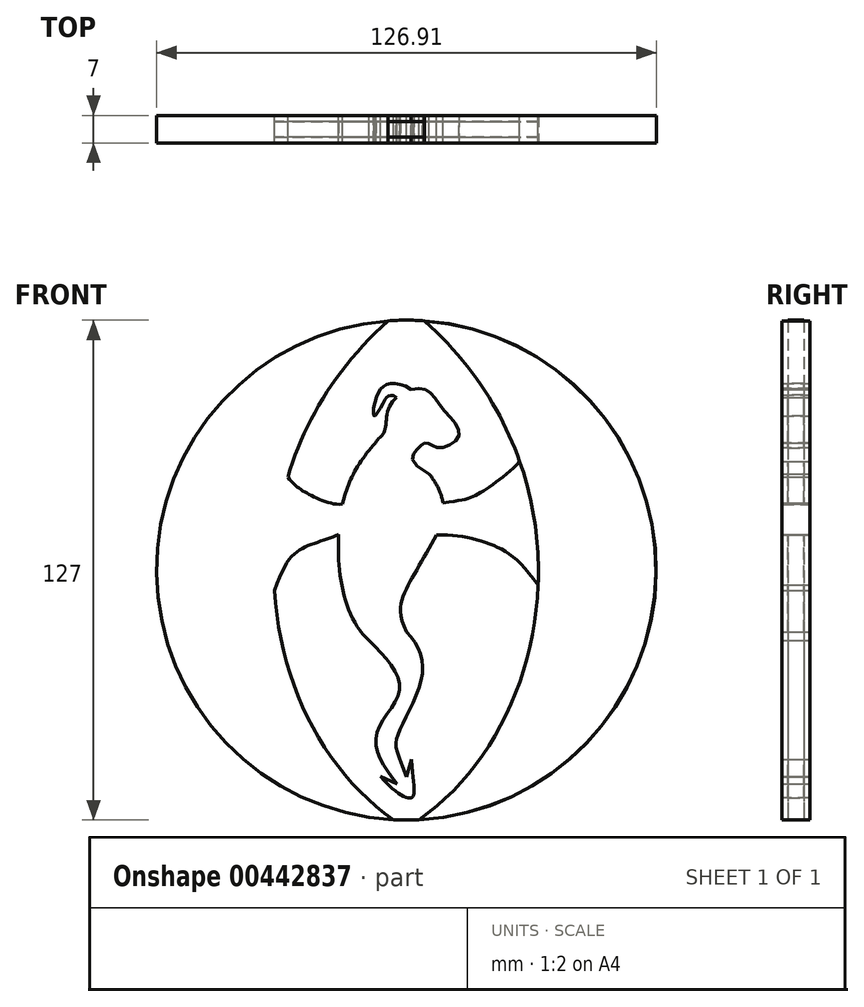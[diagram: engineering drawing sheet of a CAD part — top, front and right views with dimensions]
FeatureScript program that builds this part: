
annotation { "Feature Type Name" : "Feature", "Feature Type Description" : "" }
export const myFeature = defineFeature(function(context is Context, id is Id, definition is map)
    precondition{}
    {
        {
            var Q0;
            Q0=qCreatedBy(makeId("Front.planeOp"),FACE);
            var sketch = newSketch(context, id + "F0", { "sketchPlane" : qUnion([Q0])});
            skFitSpline(sketch, "E0", {"points": [v(-4.63, 63.33) * mm, v(-3.25, -63.42) * mm], "startDerivative": vector(-131.7, -118.32) * mm, "endDerivative": vector(104.02, -72.51) * mm});
            skFitSpline(sketch, "E1.MirrorCS", {"points": [v(4.63, 63.33) * mm, v(3.25, -63.42) * mm], "startDerivative": vector(131.7, -118.32) * mm, "endDerivative": vector(-104.02, -72.51) * mm});
            skFitSpline(sketch, "E2.MirrorCS", {"points": [v(4.63, 63.33) * mm, v(3.25, -63.42) * mm], "startDerivative": vector(131.7, -118.32) * mm, "endDerivative": vector(-104.02, -72.51) * mm});
            skFitSpline(sketch, "E3", {"points": [v(-7.83, 32.3) * mm, v(-17.25, 7.4) * mm, v(-9.48, -17.82) * mm], "startDerivative": vector(-42.51, -46.16) * mm, "endDerivative": vector(37.02, -32.66) * mm});
            skFitSpline(sketch, "E4", {"points": [v(0, -15.67) * mm, v(0, -4.86) * mm, v(6.45, 6.64) * mm, v(5.82, 24.48) * mm], "startDerivative": vector(-23.7, 51.33) * mm, "endDerivative": vector(-47.57, 61.34) * mm});
            skFitSpline(sketch, "E5", {"points": [v(-9.48, -17.82) * mm, v(-1.7, -30.34) * mm, v(-7.58, -41.9) * mm, v(-2.33, -54.32) * mm], "startDerivative": vector(35.97, -36.32) * mm, "endDerivative": vector(29.4, -36.63) * mm});
            skFitSpline(sketch, "E6", {"points": [v(0, -15.67) * mm, v(3.98, -26.92) * mm, v(-2.09, -41.71) * mm, v(0, -52.52) * mm], "startDerivative": vector(29.36, -30.45) * mm, "endDerivative": vector(25.51, -67.43) * mm});
            skLineSegment(sketch, "E7", {"start": v(-2.33, -54.32) * mm, "end": v(-6.5, -52.43) * mm});
            skLineSegment(sketch, "E8", {"start": v(0, -52.52) * mm, "end": v(1.33, -48.14) * mm});
            skFitSpline(sketch, "E9", {"points": [v(1.33, -48.14) * mm, v(1.33, -57.83) * mm, v(-6.5, -52.43) * mm], "startDerivative": vector(3.4, -40.84) * mm, "endDerivative": vector(-24.27, 27.98) * mm});
            skFitSpline(sketch, "E10", {"points": [v(-7.83, 32.3) * mm, v(-5.62, 34.96) * mm, v(-3.92, 42.22) * mm, v(4.16, 46.08) * mm, v(9.11, 41.2) * mm, v(13.41, 34.31) * mm, v(8.38, 31.08) * mm, v(5.3, 32.3) * mm, v(2.72, 30.66) * mm, v(5.82, 24.48) * mm], "startDerivative": vector(21.81, 45.2) * mm, "endDerivative": vector(144.1, -69.65) * mm});
            skFitSpline(sketch, "E11", {"points": [v(-16.2, 16.75) * mm, v(-24.84, 19.34) * mm, v(-30.09, 23.68) * mm], "startDerivative": vector(-16.82, -1.59) * mm, "endDerivative": vector(-11.22, 15.25) * mm});
            skFitSpline(sketch, "E12", {"points": [v(-17.2, 9.09) * mm, v(-24.84, 6.26) * mm, v(-33.44, -5.18) * mm], "startDerivative": vector(-15, -8.06) * mm, "endDerivative": vector(-14.25, -42.92) * mm});
            skFitSpline(sketch, "E13", {"points": [v(9.33, 17.07) * mm, v(18.58, 19.53) * mm, v(28.82, 27.58) * mm], "startDerivative": vector(36.83, 4.77) * mm, "endDerivative": vector(17.6, 18.89) * mm});
            skFitSpline(sketch, "E14", {"points": [v(7.7, 8.96) * mm, v(21.23, 6.64) * mm, v(33.5, -3.83) * mm], "startDerivative": vector(32.17, 0.55) * mm, "endDerivative": vector(27.66, -39.22) * mm});
            skFitSpline(sketch, "E15", {"points": [v(1.25, 45.88) * mm, v(-5, 47.14) * mm, v(-7.56, 44.07) * mm, v(-8.14, 39.17) * mm, v(-5.58, 42.97) * mm, v(-4.42, 44.27) * mm, v(-2.47, 43.9) * mm], "startDerivative": vector(-33.98, 22.97) * mm, "endDerivative": vector(16.3, -16.51) * mm});
            skArc(sketch, "E16", {"start": v(-4.63, 63.33) * mm, "mid": v(-63.41, -0.7) * mm, "end": v(-3.25, -63.42) * mm});
            skArc(sketch, "E17.MirrorCS", {"start": v(4.63, 63.33) * mm, "mid": v(63.41, -0.7) * mm, "end": v(3.25, -63.42) * mm});
            skCircle(sketch, "E18", {"center": v(0, 0) * mm, "radius": 63.5 * mm});
            skSolve(sketch);
        }
        {
            var Q0;
            {var subQ7=sQuery(id+"F0.wireOp",EDGE,"E11");Q0=makeQuery(id+"F0.imprint","IMPRINT",FACE,{"disambiguationData":[TD([[makeQuery(id+"F0.imprint","IMPRINT",EDGE,{"derivedFrom":subQ7}),-1.0]])]});}
            var Q1;
            {var subQ1=sQuery(id+"F0.wireOp",EDGE,"E5");Q1=makeQuery(id+"F0.imprint","IMPRINT",FACE,{"disambiguationData":[TD([[makeQuery(id+"F0.imprint","IMPRINT",EDGE,{"derivedFrom":subQ1}),-1.0]])]});}
            var Q2;
            Q2=sQuery(id+"F0.wireOp",EDGE,"E0");
            var Q3;
            Q3=sQuery(id+"F0.wireOp",EDGE,"E16");
            extrude(context, id + "F1", {"entities" : qUnion([Q0, Q1]), "surfaceEntities" : qUnion([Q2, Q3]), "endBound" : BoundingType.SYMMETRIC, "depth" : 4 * mm, "offsetDistance" : 25.4 * mm});
        }
        {
            var Q0;
            {var subQ1=sQuery(id+"F0.wireOp",EDGE,"E16");Q0=makeQuery(id+"F0.imprint","IMPRINT",FACE,{"disambiguationData":[TD([[makeQuery(id+"F0.imprint","IMPRINT",EDGE,{"derivedFrom":subQ1}),1.0]])]});}
            var Q1;
            {var subQ1=sQuery(id+"F0.wireOp",EDGE,"E17.MirrorCS");Q1=makeQuery(id+"F0.imprint","IMPRINT",FACE,{"disambiguationData":[TD([[makeQuery(id+"F0.imprint","IMPRINT",EDGE,{"derivedFrom":subQ1}),-1.0]])]});}
            var Q2;
            {var subQ0=sQuery(id+"F0.wireOp",EDGE,"E13");Q2=makeQuery(id+"F0.imprint","IMPRINT",FACE,{"disambiguationData":[TD([[makeQuery(id+"F0.imprint","IMPRINT",EDGE,{"derivedFrom":subQ0}),-1.0]])]});}
            var Q3;
            {var subQ0=sQuery(id+"F0.wireOp",EDGE,"E11");Q3=makeQuery(id+"F0.imprint","IMPRINT",FACE,{"disambiguationData":[TD([[makeQuery(id+"F0.imprint","IMPRINT",EDGE,{"derivedFrom":subQ0}),1.0]])]});}
            var Q4;
            {var subQ1=sQuery(id+"F0.wireOp",EDGE,"E5");Q4=makeQuery(id+"F0.imprint","IMPRINT",FACE,{"disambiguationData":[TD([[makeQuery(id+"F0.imprint","IMPRINT",EDGE,{"derivedFrom":subQ1}),1.0]])]});}
            var Q5;
            {var subQ0=sQuery(id+"F0.wireOp",EDGE,"E15");Q5=makeQuery(id+"F0.imprint","IMPRINT",FACE,{"disambiguationData":[TD([[makeQuery(id+"F0.imprint","IMPRINT",EDGE,{"derivedFrom":subQ0}),1.0]])]});}
            extrude(context, id + "F2", {"entities" : qUnion([Q0, Q1, Q2, Q3, Q4, Q5]), "endBound" : BoundingType.SYMMETRIC, "depth" : 7 * mm, "offsetDistance" : 25.4 * mm});
        }
    });
